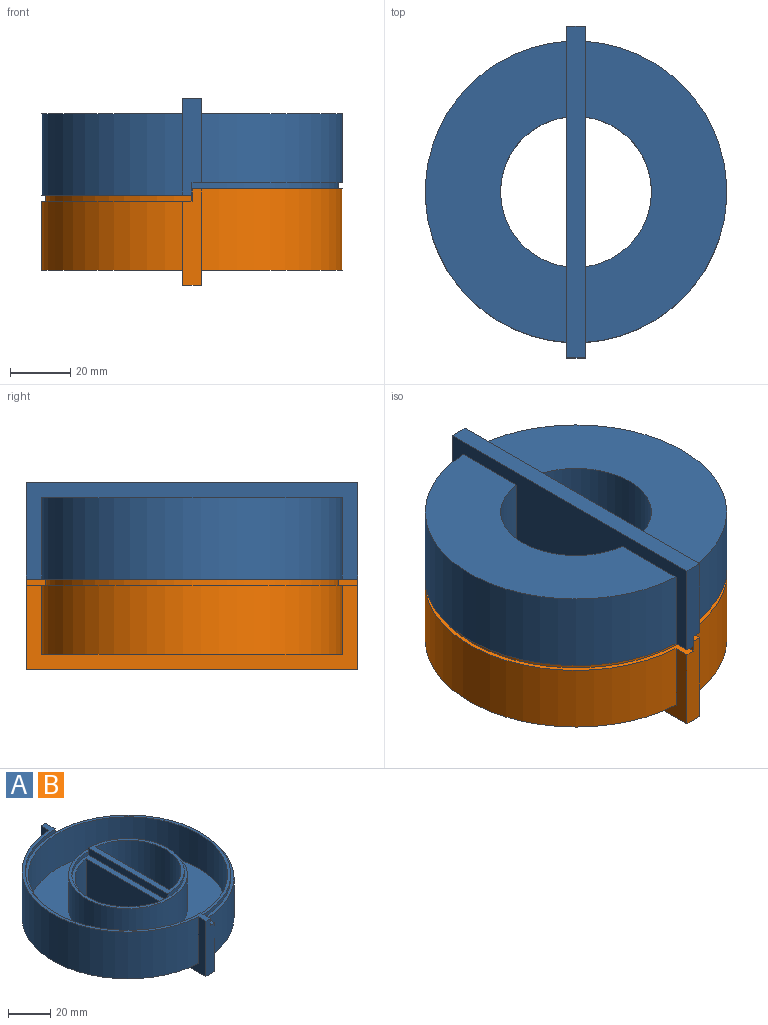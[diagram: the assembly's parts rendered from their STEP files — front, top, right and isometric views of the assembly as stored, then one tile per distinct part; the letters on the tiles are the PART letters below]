
ASSEMBLY  parts=2 mates=1
PART A: 27 faces, bbox 100x110x32 mm
  f0: plane 99.82x47mm, normal (0,0,-1), area 2795.1mm2, adj f7,f8,f10
  f1: plane 97x97mm, normal (0,0,1), area 450mm2, adj f14,f21,f24
  f2: plane 32x6mm, normal (0,-1,0), area 180mm2, adj f8,f9,f22,f23,f25,f26
  f3: plane 32x6mm, normal (0,1,0), area 180mm2, adj f8,f9,f20,f23,f25,f26
  f4: cylinder r=50mm len=99.82mm, axis (0,0,-1), area 3474.7mm2, adj f9,f12,f23
  f5: plane 53x26.5mm, normal (0,0,1), area 271mm2, adj f9,f11,f16,f19
  f6: plane 56x56mm, normal (0,0,1), area 256.8mm2, adj f13,f17,f19
  f7: cylinder r=25mm len=49.64mm, axis (0,0,-1), area 1668.1mm2, adj f0,f8,f18
  f8: plane 110x32mm, normal (-1,0,0), area 1966.6mm2, adj f0,f2,f3,f7,f10,f18,f25,f26
  f9: plane 110x32mm, normal (1,0,0), area 2124.4mm2, adj f2,f3,f4,f5,f11,f12,f23,f26
  f10: cylinder r=50mm len=99.82mm, axis (0,0,-1), area 4079.1mm2, adj f0,f8,f25
  f11: cylinder r=25mm len=49.64mm, axis (0,0,-1), area 1958.2mm2, adj f5,f9,f12
  f12: plane 99.82x47mm, normal (0,0,-1), area 2795.1mm2, adj f4,f9,f11
  f13: cylinder r=28mm len=56mm, axis (0,0,1), area 3518.6mm2, adj f6,f15
  f14: cylinder r=47mm len=94mm, axis (0,0,1), area 5906.2mm2, adj f1,f15
  f15: plane 94x94mm, normal (0,0,1), area 4476.8mm2, adj f13,f14
  f16: plane 53x4mm, normal (-1,0,0), area 212mm2, adj f5,f17,f18,f19
  f17: cylinder r=26.5mm len=53mm, axis (0,0,1), area 166.5mm2, adj f6,f16,f18
  f18: plane 53x26.5mm, normal (0,0,1), area 271mm2, adj f7,f8,f16,f17
  f19: cylinder r=26.5mm len=53mm, axis (0,0,-1), area 166.5mm2, adj f5,f6,f16
  f20: plane 6.5x4mm, normal (1,0,0), area 26mm2, adj f3,f21,f23,f24,f25
  f21: cylinder r=48.5mm len=97mm, axis (0,0,1), area 304.7mm2, adj f1,f20,f22,f23
  f22: plane 6.5x4mm, normal (1,0,0), area 26mm2, adj f2,f21,f23,f24,f25
  f23: plane 110x50mm, normal (0,0,1), area 262.3mm2, adj f2,f3,f4,f9,f20,f21,f22
  f24: cylinder r=48.5mm len=97mm, axis (0,0,-1), area 304.7mm2, adj f1,f20,f22,f25
  f25: plane 110x50mm, normal (0,0,1), area 262.3mm2, adj f2,f3,f8,f10,f20,f22,f24
  f26: plane 110x6mm, normal (0,0,-1), area 660mm2, adj f2,f3,f8,f9
PART B: same geometry as A
PLACE A rot(axis=(1,0,0),180deg) t=(96.84,-145.93,53.37)mm
PLACE B rot(axis=(0,0,1),180deg) t=(96.84,-145.93,1.37)mm
MATE fastened A.f21 <-> B.f10  axis (0,0,-1) through (96.84,-145.93,28.37)mm
